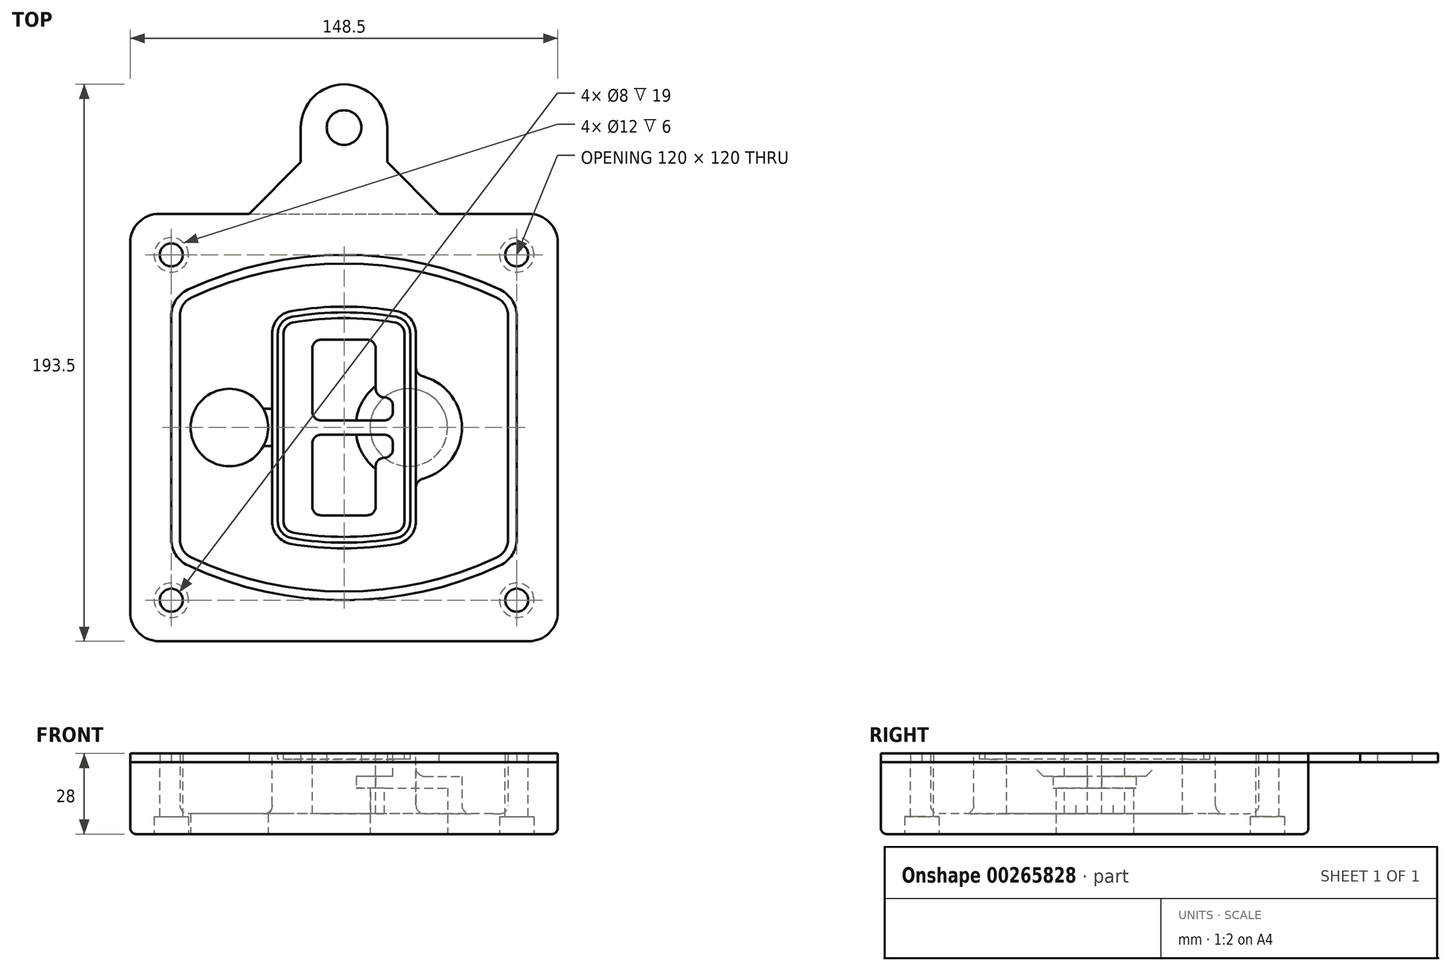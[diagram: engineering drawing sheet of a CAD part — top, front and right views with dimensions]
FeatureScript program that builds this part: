
annotation { "Feature Type Name" : "Feature", "Feature Type Description" : "" }
export const myFeature = defineFeature(function(context is Context, id is Id, definition is map)
    precondition{}
    {
        {
            var Q0;
            Q0=qCreatedBy(makeId("Top.planeOp"),FACE);
            var sketch = newSketch(context, id + "F0", { "sketchPlane" : qUnion([Q0])});
            skPoint(sketch, "E0.rect.middle", {"position": v(0, 0) * mm});
            skLineSegment(sketch, "E1.bottom", {"start": v(-64.25, -74.25) * mm, "end": v(64.25, -74.25) * mm});
            skLineSegment(sketch, "E1.top", {"start": v(-64.25, 74.25) * mm, "end": v(64.25, 74.25) * mm});
            skLineSegment(sketch, "E1.left", {"start": v(-74.25, -64.25) * mm, "end": v(-74.25, 64.25) * mm});
            skLineSegment(sketch, "E1.right", {"start": v(74.25, -64.25) * mm, "end": v(74.25, 64.25) * mm});
            skLineSegment(sketch, "E2", {"start": v(-74.25, 74.25) * mm, "end": v(74.25, -74.25) * mm, "construction": true});
            skLineSegment(sketch, "E3", {"start": v(74.25, 74.25) * mm, "end": v(-74.25, -74.25) * mm, "construction": true});
            skCircle(sketch, "E4", {"center": v(-60, 60) * mm, "radius": 4 * mm});
            skCircle(sketch, "E5", {"center": v(60, 60) * mm, "radius": 4 * mm});
            skCircle(sketch, "E6", {"center": v(60, -60) * mm, "radius": 4 * mm});
            skCircle(sketch, "E7", {"center": v(-60, -60) * mm, "radius": 4 * mm});
            skLineSegment(sketch, "E8", {"start": v(-60, 60) * mm, "end": v(60, 60) * mm, "construction": true});
            skLineSegment(sketch, "E9", {"start": v(60, 60) * mm, "end": v(60, -60) * mm, "construction": true});
            skLineSegment(sketch, "E10", {"start": v(60, -60) * mm, "end": v(-60, -60) * mm, "construction": true});
            skLineSegment(sketch, "E11", {"start": v(-60, -60) * mm, "end": v(-60, 60) * mm, "construction": true});
            skLineSegment(sketch, "E12", {"start": v(-60, 38.83) * mm, "end": v(-60, -38.83) * mm});
            skLineSegment(sketch, "E13", {"start": v(60, 38.83) * mm, "end": v(60, -38.83) * mm});
            skArc(sketch, "E14", {"start": v(54.26, 47.88) * mm, "mid": v(0, 60) * mm, "end": v(-54.26, 47.88) * mm});
            skArc(sketch, "E15", {"start": v(-54.26, -47.88) * mm, "mid": v(0, -60) * mm, "end": v(54.26, -47.88) * mm});
            skLineSegment(sketch, "E16", {"start": v(-60, 0) * mm, "end": v(60, 0) * mm, "construction": true});
            skPoint(sketch, "E17.visualSharp", {"position": v(-60, -45) * mm});
            skArc(sketch, "E17.filletArc", {"start": v(-60, -38.83) * mm, "mid": v(-58.44, -44.2) * mm, "end": v(-54.26, -47.88) * mm});
            skPoint(sketch, "E18.visualSharp", {"position": v(-60, 45) * mm});
            skArc(sketch, "E18.filletArc", {"start": v(-54.26, 47.88) * mm, "mid": v(-58.44, 44.2) * mm, "end": v(-60, 38.83) * mm});
            skPoint(sketch, "E19.visualSharp", {"position": v(60, 45) * mm});
            skArc(sketch, "E19.filletArc", {"start": v(60, 38.83) * mm, "mid": v(58.44, 44.2) * mm, "end": v(54.26, 47.88) * mm});
            skPoint(sketch, "E20.visualSharp", {"position": v(60, -45) * mm});
            skArc(sketch, "E20.filletArc", {"start": v(54.26, -47.88) * mm, "mid": v(58.44, -44.2) * mm, "end": v(60, -38.83) * mm});
            skPoint(sketch, "E21.visualSharp", {"position": v(-74.25, 74.25) * mm});
            skArc(sketch, "E21.filletArc", {"start": v(-64.25, 74.25) * mm, "mid": v(-71.32, 71.32) * mm, "end": v(-74.25, 64.25) * mm});
            skPoint(sketch, "E22.visualSharp", {"position": v(74.25, 74.25) * mm});
            skArc(sketch, "E22.filletArc", {"start": v(74.25, 64.25) * mm, "mid": v(71.32, 71.32) * mm, "end": v(64.25, 74.25) * mm});
            skPoint(sketch, "E23.visualSharp", {"position": v(74.25, -74.25) * mm});
            skArc(sketch, "E23.filletArc", {"start": v(64.25, -74.25) * mm, "mid": v(71.32, -71.32) * mm, "end": v(74.25, -64.25) * mm});
            skPoint(sketch, "E24.visualSharp", {"position": v(-74.25, -74.25) * mm});
            skArc(sketch, "E24.filletArc", {"start": v(-74.25, -64.25) * mm, "mid": v(-71.32, -71.32) * mm, "end": v(-64.25, -74.25) * mm});
            skArc(sketch, "E25.0", {"start": v(57, 38.83) * mm, "mid": v(55.9, 42.58) * mm, "end": v(52.98, 45.17) * mm});
            skLineSegment(sketch, "E25.1", {"start": v(57, 38.83) * mm, "end": v(57, -38.83) * mm});
            skArc(sketch, "E25.2", {"start": v(52.98, -45.17) * mm, "mid": v(55.9, -42.58) * mm, "end": v(57, -38.83) * mm});
            skArc(sketch, "E25.3", {"start": v(-52.98, -45.17) * mm, "mid": v(0, -57) * mm, "end": v(52.98, -45.17) * mm});
            skArc(sketch, "E25.4", {"start": v(-57, -38.83) * mm, "mid": v(-55.9, -42.58) * mm, "end": v(-52.98, -45.17) * mm});
            skArc(sketch, "E25.5", {"start": v(52.98, 45.17) * mm, "mid": v(0, 57) * mm, "end": v(-52.98, 45.17) * mm});
            skLineSegment(sketch, "E25.6", {"start": v(-57, 38.83) * mm, "end": v(-57, -38.83) * mm});
            skArc(sketch, "E25.7", {"start": v(-52.98, 45.17) * mm, "mid": v(-55.9, 42.58) * mm, "end": v(-57, 38.83) * mm});
            skArc(sketch, "E26.0", {"start": v(-55.96, 51.5) * mm, "mid": v(-61.82, 46.33) * mm, "end": v(-64, 38.83) * mm});
            skArc(sketch, "E26.1", {"start": v(55.96, 51.5) * mm, "mid": v(0, 64) * mm, "end": v(-55.96, 51.5) * mm});
            skArc(sketch, "E26.2", {"start": v(64, 38.83) * mm, "mid": v(61.82, 46.33) * mm, "end": v(55.96, 51.5) * mm});
            skLineSegment(sketch, "E26.3", {"start": v(64, 38.83) * mm, "end": v(64, -38.83) * mm});
            skArc(sketch, "E26.4", {"start": v(55.96, -51.5) * mm, "mid": v(61.82, -46.33) * mm, "end": v(64, -38.83) * mm});
            skLineSegment(sketch, "E26.5", {"start": v(-64, 38.83) * mm, "end": v(-64, -38.83) * mm});
            skArc(sketch, "E26.6", {"start": v(-55.96, -51.5) * mm, "mid": v(0, -64) * mm, "end": v(55.96, -51.5) * mm});
            skArc(sketch, "E26.7", {"start": v(-64, -38.83) * mm, "mid": v(-61.82, -46.33) * mm, "end": v(-55.96, -51.5) * mm});
            skSolve(sketch);
        }
        {
            var Q0;
            Q0=makeQuery(id+"F0.imprint","IMPRINT",FACE,{"disambiguationData":[TD([[makeQuery(id+"F0.imprint","IMPRINT",EDGE,{"derivedFrom":sQuery(id+"F0.wireOp",EDGE,"E1.bottom")}),1.0]])]});
            var Q1;
            Q1=makeQuery(id+"F0.imprint","IMPRINT",FACE,{"disambiguationData":[TD([[makeQuery(id+"F0.imprint","IMPRINT",EDGE,{"derivedFrom":sQuery(id+"F0.wireOp",EDGE,"E12")}),1.0]])]});
            var Q2;
            Q2=makeQuery(id+"F0.imprint","IMPRINT",FACE,{"disambiguationData":[TD([[makeQuery(id+"F0.imprint","IMPRINT",EDGE,{"derivedFrom":sQuery(id+"F0.wireOp",EDGE,"E25.0")}),1.0]])]});
            var Q3;
            Q3=makeQuery(id+"F0.imprint","IMPRINT",FACE,{"disambiguationData":[TD([[makeQuery(id+"F0.imprint","IMPRINT",EDGE,{"derivedFrom":sQuery(id+"F0.wireOp",EDGE,"E12")}),-1.0]])]});
            extrude(context, id + "F1", {"entities" : qUnion([Q0, Q1, Q2, Q3]), "oppositeDirection" : true, "depth" : 25 * mm});
        }
        {
            var Q0;
            Q0=makeQuery(id+"F0.imprint","IMPRINT",FACE,{"disambiguationData":[TD([[makeQuery(id+"F0.imprint","IMPRINT",EDGE,{"derivedFrom":sQuery(id+"F0.wireOp",EDGE,"E12")}),1.0]])]});
            extrude(context, id + "F2", {"entities" : qUnion([Q0]), "operationType" : NewBodyOperationType.ADD, "depth" : 3 * mm});
        }
        {
            var Q0;
            Q0=makeQuery(id+"F0.imprint","IMPRINT",FACE,{"disambiguationData":[TD([[makeQuery(id+"F0.imprint","IMPRINT",EDGE,{"derivedFrom":sQuery(id+"F0.wireOp",EDGE,"E25.0")}),1.0]])]});
            extrude(context, id + "F3", {"entities" : qUnion([Q0]), "operationType" : NewBodyOperationType.REMOVE, "oppositeDirection" : true, "depth" : 18 * mm});
        }
        {
            var Q0;
            Q0=makeQuery(id+"F2.opExtrude","CAP_FACE",FACE,{"disambiguationData":[OSD([sQuery(id+"F0.wireOp",EDGE,"E12"),sQuery(id+"F0.wireOp",EDGE,"E13"),sQuery(id+"F0.wireOp",EDGE,"E14"),sQuery(id+"F0.wireOp",EDGE,"E15"),sQuery(id+"F0.wireOp",EDGE,"E17.filletArc"),sQuery(id+"F0.wireOp",EDGE,"E18.filletArc"),sQuery(id+"F0.wireOp",EDGE,"E19.filletArc"),sQuery(id+"F0.wireOp",EDGE,"E20.filletArc"),sQuery(id+"F0.wireOp",EDGE,"E25.0"),sQuery(id+"F0.wireOp",EDGE,"E25.1"),sQuery(id+"F0.wireOp",EDGE,"E25.2"),sQuery(id+"F0.wireOp",EDGE,"E25.3"),sQuery(id+"F0.wireOp",EDGE,"E25.4"),sQuery(id+"F0.wireOp",EDGE,"E25.5"),sQuery(id+"F0.wireOp",EDGE,"E25.6"),sQuery(id+"F0.wireOp",EDGE,"E25.7")])],"isStart":false});
            var sketch = newSketch(context, id + "F4", { "sketchPlane" : qUnion([Q0])});
            skArc(sketch, "E27.0", {"start": v(-18.34, -40.45) * mm, "mid": v(0, -42) * mm, "end": v(18.34, -40.45) * mm});
            skArc(sketch, "E28.0", {"start": v(18.34, 40.45) * mm, "mid": v(0, 42) * mm, "end": v(-18.34, 40.45) * mm});
            skLineSegment(sketch, "E29", {"start": v(-25, 32.57) * mm, "end": v(-25, -32.57) * mm});
            skLineSegment(sketch, "E30", {"start": v(25, 32.57) * mm, "end": v(25, -32.57) * mm});
            skLineSegment(sketch, "E31", {"start": v(-25, 39.1) * mm, "end": v(25, 39.1) * mm, "construction": true});
            skLineSegment(sketch, "E32", {"start": v(-25, -39.1) * mm, "end": v(25, -39.1) * mm, "construction": true});
            skPoint(sketch, "E33.visualSharp", {"position": v(-25, 39.1) * mm});
            skArc(sketch, "E33.filletArc", {"start": v(-18.34, 40.45) * mm, "mid": v(-23.11, 37.73) * mm, "end": v(-25, 32.57) * mm});
            skPoint(sketch, "E34.visualSharp", {"position": v(25, 39.1) * mm});
            skArc(sketch, "E34.filletArc", {"start": v(25, 32.57) * mm, "mid": v(23.11, 37.73) * mm, "end": v(18.34, 40.45) * mm});
            skPoint(sketch, "E35.visualSharp", {"position": v(25, -39.1) * mm});
            skArc(sketch, "E35.filletArc", {"start": v(18.34, -40.45) * mm, "mid": v(23.11, -37.73) * mm, "end": v(25, -32.57) * mm});
            skPoint(sketch, "E36.visualSharp", {"position": v(-25, -39.1) * mm});
            skArc(sketch, "E36.filletArc", {"start": v(-25, -32.57) * mm, "mid": v(-23.11, -37.73) * mm, "end": v(-18.34, -40.45) * mm});
            skArc(sketch, "E37.0", {"start": v(52.98, 45.17) * mm, "mid": v(0, 57) * mm, "end": v(-52.98, 45.17) * mm});
            skArc(sketch, "E37.1", {"start": v(-52.98, 45.17) * mm, "mid": v(-55.9, 42.58) * mm, "end": v(-57, 38.83) * mm});
            skLineSegment(sketch, "E37.2", {"start": v(-57, 38.83) * mm, "end": v(-57, -38.83) * mm});
            skArc(sketch, "E37.3", {"start": v(-57, -38.83) * mm, "mid": v(-55.9, -42.58) * mm, "end": v(-52.98, -45.17) * mm});
            skArc(sketch, "E37.4", {"start": v(-52.98, -45.17) * mm, "mid": v(0, -57) * mm, "end": v(52.98, -45.17) * mm});
            skArc(sketch, "E37.5", {"start": v(52.98, -45.17) * mm, "mid": v(55.9, -42.58) * mm, "end": v(57, -38.83) * mm});
            skLineSegment(sketch, "E37.6", {"start": v(57, 38.83) * mm, "end": v(57, -38.83) * mm});
            skArc(sketch, "E37.7", {"start": v(57, 38.83) * mm, "mid": v(55.9, 42.58) * mm, "end": v(52.98, 45.17) * mm});
            skLineSegment(sketch, "E38.0", {"start": v(23, 32.57) * mm, "end": v(23, -32.57) * mm});
            skArc(sketch, "E38.1", {"start": v(18, -38.48) * mm, "mid": v(21.58, -36.44) * mm, "end": v(23, -32.57) * mm});
            skArc(sketch, "E38.2", {"start": v(-18, -38.48) * mm, "mid": v(0, -40) * mm, "end": v(18, -38.48) * mm});
            skArc(sketch, "E38.3", {"start": v(-23, -32.57) * mm, "mid": v(-21.58, -36.44) * mm, "end": v(-18, -38.48) * mm});
            skLineSegment(sketch, "E38.4", {"start": v(-23, 32.57) * mm, "end": v(-23, -32.57) * mm});
            skArc(sketch, "E38.5", {"start": v(23, 32.57) * mm, "mid": v(21.58, 36.44) * mm, "end": v(18, 38.48) * mm});
            skArc(sketch, "E38.6", {"start": v(-18, 38.48) * mm, "mid": v(-21.58, 36.44) * mm, "end": v(-23, 32.57) * mm});
            skArc(sketch, "E38.7", {"start": v(18, 38.48) * mm, "mid": v(0, 40) * mm, "end": v(-18, 38.48) * mm});
            skArc(sketch, "E39.0", {"start": v(21, 32.57) * mm, "mid": v(20.06, 35.15) * mm, "end": v(17.67, 36.5) * mm});
            skLineSegment(sketch, "E39.1", {"start": v(21, 32.57) * mm, "end": v(21, -32.57) * mm});
            skArc(sketch, "E39.2", {"start": v(17.67, -36.5) * mm, "mid": v(20.06, -35.15) * mm, "end": v(21, -32.57) * mm});
            skArc(sketch, "E39.3", {"start": v(-17.67, -36.5) * mm, "mid": v(0, -38) * mm, "end": v(17.67, -36.5) * mm});
            skArc(sketch, "E39.4", {"start": v(-21, -32.57) * mm, "mid": v(-20.06, -35.15) * mm, "end": v(-17.67, -36.5) * mm});
            skArc(sketch, "E39.5", {"start": v(17.67, 36.5) * mm, "mid": v(0, 38) * mm, "end": v(-17.67, 36.5) * mm});
            skLineSegment(sketch, "E39.6", {"start": v(-21, 32.57) * mm, "end": v(-21, -32.57) * mm});
            skArc(sketch, "E39.7", {"start": v(-17.67, 36.5) * mm, "mid": v(-20.06, 35.15) * mm, "end": v(-21, 32.57) * mm});
            skLineSegment(sketch, "E40", {"start": v(-25, 0) * mm, "end": v(25, 0) * mm, "construction": true});
            skLineSegment(sketch, "E41", {"start": v(-11, 5.5) * mm, "end": v(-11, 27.5) * mm});
            skLineSegment(sketch, "E42", {"start": v(-8, 30.5) * mm, "end": v(8, 30.5) * mm});
            skLineSegment(sketch, "E43", {"start": v(11, 27.5) * mm, "end": v(11, 13.5) * mm});
            skLineSegment(sketch, "E44", {"start": v(14, 10.5) * mm, "end": v(14, 10.5) * mm});
            skLineSegment(sketch, "E45", {"start": v(17, 7.5) * mm, "end": v(17, 5.5) * mm});
            skLineSegment(sketch, "E46", {"start": v(14, 2.5) * mm, "end": v(-8, 2.5) * mm});
            skPoint(sketch, "E47.visualSharp", {"position": v(-11, 30.5) * mm});
            skArc(sketch, "E47.filletArc", {"start": v(-8, 30.5) * mm, "mid": v(-10.12, 29.62) * mm, "end": v(-11, 27.5) * mm});
            skPoint(sketch, "E48.visualSharp", {"position": v(11, 30.5) * mm});
            skArc(sketch, "E48.filletArc", {"start": v(11, 27.5) * mm, "mid": v(10.12, 29.62) * mm, "end": v(8, 30.5) * mm});
            skPoint(sketch, "E49.visualSharp", {"position": v(11, 10.5) * mm});
            skArc(sketch, "E49.filletArc", {"start": v(11, 13.5) * mm, "mid": v(11.88, 11.38) * mm, "end": v(14, 10.5) * mm});
            skPoint(sketch, "E50.visualSharp", {"position": v(17, 10.5) * mm});
            skArc(sketch, "E50.filletArc", {"start": v(17, 7.5) * mm, "mid": v(16.12, 9.62) * mm, "end": v(14, 10.5) * mm});
            skPoint(sketch, "E51.visualSharp", {"position": v(17, 2.5) * mm});
            skArc(sketch, "E51.filletArc", {"start": v(14, 2.5) * mm, "mid": v(16.12, 3.38) * mm, "end": v(17, 5.5) * mm});
            skPoint(sketch, "E52.visualSharp", {"position": v(-11, 2.5) * mm});
            skArc(sketch, "E52.filletArc", {"start": v(-11, 5.5) * mm, "mid": v(-10.12, 3.38) * mm, "end": v(-8, 2.5) * mm});
            skLineSegment(sketch, "E53.0.MirrorCS", {"start": v(14, -2.5) * mm, "end": v(-8, -2.5) * mm});
            skArc(sketch, "E54.0.MirrorCS", {"start": v(-11, -5.5) * mm, "mid": v(-10.12, -3.38) * mm, "end": v(-8, -2.5) * mm});
            skLineSegment(sketch, "E55.0.MirrorCS", {"start": v(-11, -5.5) * mm, "end": v(-11, -27.5) * mm});
            skArc(sketch, "E56.0.MirrorCS", {"start": v(-8, -30.5) * mm, "mid": v(-10.12, -29.62) * mm, "end": v(-11, -27.5) * mm});
            skLineSegment(sketch, "E57.0.MirrorCS", {"start": v(-8, -30.5) * mm, "end": v(8, -30.5) * mm});
            skArc(sketch, "E58.0.MirrorCS", {"start": v(11, -27.5) * mm, "mid": v(10.12, -29.62) * mm, "end": v(8, -30.5) * mm});
            skLineSegment(sketch, "E59.0.MirrorCS", {"start": v(11, -27.5) * mm, "end": v(11, -13.5) * mm});
            skArc(sketch, "E60.0.MirrorCS", {"start": v(11, -13.5) * mm, "mid": v(11.88, -11.38) * mm, "end": v(14, -10.5) * mm});
            skArc(sketch, "E61.0.MirrorCS", {"start": v(17, -7.5) * mm, "mid": v(16.12, -9.62) * mm, "end": v(14, -10.5) * mm});
            skLineSegment(sketch, "E62.0.MirrorCS", {"start": v(17, -7.5) * mm, "end": v(17, -5.5) * mm});
            skArc(sketch, "E63.0.MirrorCS", {"start": v(14, -2.5) * mm, "mid": v(16.12, -3.38) * mm, "end": v(17, -5.5) * mm});
            skSolve(sketch);
        }
        {
            var Q0;
            Q0=makeQuery(id+"F4.imprint","IMPRINT",FACE,{"disambiguationData":[TD([[makeQuery(id+"F4.imprint","IMPRINT",EDGE,{"derivedFrom":sQuery(id+"F4.wireOp",EDGE,"E27.0")}),1.0]])]});
            var Q1;
            Q1=makeQuery(id+"F4.imprint","IMPRINT",FACE,{"disambiguationData":[TD([[makeQuery(id+"F4.imprint","IMPRINT",EDGE,{"derivedFrom":sQuery(id+"F4.wireOp",EDGE,"E38.0")}),-1.0]])]});
            var Q2;
            Q2=makeQuery(id+"F4.imprint","IMPRINT",FACE,{"disambiguationData":[TD([[makeQuery(id+"F4.imprint","IMPRINT",EDGE,{"derivedFrom":sQuery(id+"F4.wireOp",EDGE,"E39.0")}),1.0]])]});
            extrude(context, id + "F5", {"entities" : qUnion([Q0, Q1, Q2]), "operationType" : NewBodyOperationType.ADD, "endBound" : BoundingType.UP_TO_NEXT, "oppositeDirection" : true, "depth" : 25 * mm});
        }
        {
            var Q0;
            Q0=makeQuery(id+"F4.imprint","IMPRINT",FACE,{"disambiguationData":[TD([[makeQuery(id+"F4.imprint","IMPRINT",EDGE,{"derivedFrom":sQuery(id+"F4.wireOp",EDGE,"E38.0")}),-1.0]])]});
            extrude(context, id + "F6", {"entities" : qUnion([Q0]), "operationType" : NewBodyOperationType.REMOVE, "oppositeDirection" : true, "depth" : 2 * mm});
        }
        {
            var Q0;
            Q0=makeQuery(id+"F1.opExtrude","CAP_FACE",FACE,{"disambiguationData":[OSD([sQuery(id+"F0.wireOp",EDGE,"E1.bottom"),sQuery(id+"F0.wireOp",EDGE,"E1.top"),sQuery(id+"F0.wireOp",EDGE,"E1.left"),sQuery(id+"F0.wireOp",EDGE,"E1.right"),sQuery(id+"F0.wireOp",EDGE,"E4"),sQuery(id+"F0.wireOp",EDGE,"E5"),sQuery(id+"F0.wireOp",EDGE,"E6"),sQuery(id+"F0.wireOp",EDGE,"E7"),sQuery(id+"F0.wireOp",EDGE,"E21.filletArc"),sQuery(id+"F0.wireOp",EDGE,"E22.filletArc"),sQuery(id+"F0.wireOp",EDGE,"E23.filletArc"),sQuery(id+"F0.wireOp",EDGE,"E24.filletArc")])],"isStart":false});
            var sketch = newSketch(context, id + "F7", { "sketchPlane" : qUnion([Q0])});
            skCircle(sketch, "E64", {"center": v(22.5, 0) * mm, "radius": 13.47 * mm});
            skCircle(sketch, "E65", {"center": v(-39.81, 0) * mm, "radius": 13.47 * mm});
            skLineSegment(sketch, "E66", {"start": v(74.25, 0) * mm, "end": v(-74.25, 0) * mm});
            skCircle(sketch, "E67", {"center": v(22.5, 0) * mm, "radius": 18.47 * mm});
            skCircle(sketch, "E68", {"center": v(60, -60) * mm, "radius": 6 * mm});
            skCircle(sketch, "E69", {"center": v(-60, -60) * mm, "radius": 6 * mm});
            skCircle(sketch, "E70", {"center": v(-60, 60) * mm, "radius": 6 * mm});
            skCircle(sketch, "E71", {"center": v(60, 60) * mm, "radius": 6 * mm});
            skSolve(sketch);
        }
        {
            var Q0;
            {var subQ1=sQuery(id+"F7.wireOp",EDGE,"E66");var subQ4=sQuery(id+"F7.wireOp",EDGE,"E64");var subQ6=makeQuery(id+"F7.imprint","INTERSECT",VERTEX,{"disambiguationData":[OD(0.0)],"derivedFrom":[subQ4,subQ1]});Q0=makeQuery(id+"F7.imprint","IMPRINT",FACE,{"disambiguationData":[TD([[makeQuery(id+"F7.imprint","IMPRINT",EDGE,{"disambiguationData":[TD([[subQ6,-1.0]])],"derivedFrom":subQ4}),-1.0]])]});}
            var Q1;
            {var subQ0=sQuery(id+"F7.wireOp",EDGE,"E66");var subQ1=sQuery(id+"F7.wireOp",EDGE,"E64");var subQ3=makeQuery(id+"F7.imprint","INTERSECT",VERTEX,{"disambiguationData":[OD(0.0)],"derivedFrom":[subQ1,subQ0]});Q1=makeQuery(id+"F7.imprint","IMPRINT",FACE,{"disambiguationData":[TD([[makeQuery(id+"F7.imprint","IMPRINT",EDGE,{"disambiguationData":[TD([[subQ3,-1.0]])],"derivedFrom":subQ1}),1.0]])]});}
            var Q2;
            {var subQ0=sQuery(id+"F7.wireOp",EDGE,"E66");var subQ1=sQuery(id+"F7.wireOp",EDGE,"E64");var subQ3=makeQuery(id+"F7.imprint","INTERSECT",VERTEX,{"disambiguationData":[OD(0.0)],"derivedFrom":[subQ1,subQ0]});Q2=makeQuery(id+"F7.imprint","IMPRINT",FACE,{"disambiguationData":[TD([[makeQuery(id+"F7.imprint","IMPRINT",EDGE,{"disambiguationData":[TD([[subQ3,1.0]])],"derivedFrom":subQ1}),1.0]])]});}
            var Q3;
            {var subQ1=sQuery(id+"F7.wireOp",EDGE,"E66");var subQ4=sQuery(id+"F7.wireOp",EDGE,"E64");var subQ6=makeQuery(id+"F7.imprint","INTERSECT",VERTEX,{"disambiguationData":[OD(0.0)],"derivedFrom":[subQ4,subQ1]});Q3=makeQuery(id+"F7.imprint","IMPRINT",FACE,{"disambiguationData":[TD([[makeQuery(id+"F7.imprint","IMPRINT",EDGE,{"disambiguationData":[TD([[subQ6,1.0]])],"derivedFrom":subQ4}),-1.0]])]});}
            extrude(context, id + "F8", {"entities" : qUnion([Q0, Q1, Q2, Q3]), "operationType" : NewBodyOperationType.ADD, "oppositeDirection" : true, "depth" : 20 * mm});
        }
        {
            var Q0;
            {var subQ0=sQuery(id+"F7.wireOp",EDGE,"E66");var subQ1=sQuery(id+"F7.wireOp",EDGE,"E64");var subQ3=makeQuery(id+"F7.imprint","INTERSECT",VERTEX,{"disambiguationData":[OD(0.0)],"derivedFrom":[subQ1,subQ0]});Q0=makeQuery(id+"F7.imprint","IMPRINT",FACE,{"disambiguationData":[TD([[makeQuery(id+"F7.imprint","IMPRINT",EDGE,{"disambiguationData":[TD([[subQ3,-1.0]])],"derivedFrom":subQ1}),1.0]])]});}
            var Q1;
            {var subQ0=sQuery(id+"F7.wireOp",EDGE,"E66");var subQ1=sQuery(id+"F7.wireOp",EDGE,"E64");var subQ3=makeQuery(id+"F7.imprint","INTERSECT",VERTEX,{"disambiguationData":[OD(0.0)],"derivedFrom":[subQ1,subQ0]});Q1=makeQuery(id+"F7.imprint","IMPRINT",FACE,{"disambiguationData":[TD([[makeQuery(id+"F7.imprint","IMPRINT",EDGE,{"disambiguationData":[TD([[subQ3,1.0]])],"derivedFrom":subQ1}),1.0]])]});}
            extrude(context, id + "F9", {"entities" : qUnion([Q0, Q1]), "operationType" : NewBodyOperationType.REMOVE, "oppositeDirection" : true, "depth" : 16 * mm});
        }
        {
            var Q0;
            {var subQ0=sQuery(id+"F7.wireOp",EDGE,"E66");var subQ1=sQuery(id+"F7.wireOp",EDGE,"E65");var subQ3=makeQuery(id+"F7.imprint","INTERSECT",VERTEX,{"disambiguationData":[OD(0.0)],"derivedFrom":[subQ1,subQ0]});Q0=makeQuery(id+"F7.imprint","IMPRINT",FACE,{"disambiguationData":[TD([[makeQuery(id+"F7.imprint","IMPRINT",EDGE,{"disambiguationData":[TD([[subQ3,-1.0]])],"derivedFrom":subQ1}),1.0]])]});}
            var Q1;
            {var subQ0=sQuery(id+"F7.wireOp",EDGE,"E66");var subQ1=sQuery(id+"F7.wireOp",EDGE,"E65");var subQ3=makeQuery(id+"F7.imprint","INTERSECT",VERTEX,{"disambiguationData":[OD(0.0)],"derivedFrom":[subQ1,subQ0]});Q1=makeQuery(id+"F7.imprint","IMPRINT",FACE,{"disambiguationData":[TD([[makeQuery(id+"F7.imprint","IMPRINT",EDGE,{"disambiguationData":[TD([[subQ3,1.0]])],"derivedFrom":subQ1}),1.0]])]});}
            extrude(context, id + "F10", {"entities" : qUnion([Q0, Q1]), "operationType" : NewBodyOperationType.REMOVE, "oppositeDirection" : true, "depth" : 25 * mm});
        }
        {
            var Q0;
            Q0=makeQuery(id+"F7.imprint","IMPRINT",FACE,{"disambiguationData":[TD([[makeQuery(id+"F7.imprint","IMPRINT",EDGE,{"derivedFrom":sQuery(id+"F7.wireOp",EDGE,"E68")}),1.0]])]});
            var Q1;
            Q1=makeQuery(id+"F7.imprint","IMPRINT",FACE,{"disambiguationData":[TD([[makeQuery(id+"F7.imprint","IMPRINT",EDGE,{"derivedFrom":makeQuery(id+"F1.opExtrude","CAP_EDGE",EDGE,{"disambiguationData":[OSD([sQuery(id+"F0.wireOp",EDGE,"E5")])],"isStart":false})}),-1.0]])]});
            var Q2;
            Q2=makeQuery(id+"F7.imprint","IMPRINT",FACE,{"disambiguationData":[TD([[makeQuery(id+"F7.imprint","IMPRINT",EDGE,{"derivedFrom":sQuery(id+"F7.wireOp",EDGE,"E69")}),1.0]])]});
            var Q3;
            Q3=makeQuery(id+"F7.imprint","IMPRINT",FACE,{"disambiguationData":[TD([[makeQuery(id+"F7.imprint","IMPRINT",EDGE,{"derivedFrom":makeQuery(id+"F1.opExtrude","CAP_EDGE",EDGE,{"disambiguationData":[OSD([sQuery(id+"F0.wireOp",EDGE,"E4")])],"isStart":false})}),-1.0]])]});
            var Q4;
            Q4=makeQuery(id+"F7.imprint","IMPRINT",FACE,{"disambiguationData":[TD([[makeQuery(id+"F7.imprint","IMPRINT",EDGE,{"derivedFrom":sQuery(id+"F7.wireOp",EDGE,"E70")}),1.0]])]});
            var Q5;
            Q5=makeQuery(id+"F7.imprint","IMPRINT",FACE,{"disambiguationData":[TD([[makeQuery(id+"F7.imprint","IMPRINT",EDGE,{"derivedFrom":makeQuery(id+"F1.opExtrude","CAP_EDGE",EDGE,{"disambiguationData":[OSD([sQuery(id+"F0.wireOp",EDGE,"E7")])],"isStart":false})}),-1.0]])]});
            var Q6;
            Q6=makeQuery(id+"F7.imprint","IMPRINT",FACE,{"disambiguationData":[TD([[makeQuery(id+"F7.imprint","IMPRINT",EDGE,{"derivedFrom":sQuery(id+"F7.wireOp",EDGE,"E71")}),1.0]])]});
            var Q7;
            Q7=makeQuery(id+"F7.imprint","IMPRINT",FACE,{"disambiguationData":[TD([[makeQuery(id+"F7.imprint","IMPRINT",EDGE,{"derivedFrom":makeQuery(id+"F1.opExtrude","CAP_EDGE",EDGE,{"disambiguationData":[OSD([sQuery(id+"F0.wireOp",EDGE,"E6")])],"isStart":false})}),-1.0]])]});
            extrude(context, id + "F11", {"entities" : qUnion([Q0, Q1, Q2, Q3, Q4, Q5, Q6, Q7]), "operationType" : NewBodyOperationType.REMOVE, "oppositeDirection" : true, "depth" : 6 * mm});
        }
        {
            var Q0;
            Q0=makeQuery(id+"F9.boolean.opBoolean","COPY",FACE,{"derivedFrom":makeQuery(id+"F9.opExtrude","CAP_FACE",FACE,{"disambiguationData":[OSD([sQuery(id+"F7.wireOp",EDGE,"E64")])],"isStart":false})});
            var sketch = newSketch(context, id + "F12", { "sketchPlane" : qUnion([Q0])});
            skArc(sketch, "E72.0", {"start": v(11, 14.45) * mm, "mid": v(6.45, 9.13) * mm, "end": v(4.2, 2.5) * mm});
            skArc(sketch, "E72.1", {"start": v(4.2, -2.5) * mm, "mid": v(6.45, -9.13) * mm, "end": v(11, -14.45) * mm});
            skLineSegment(sketch, "E73", {"start": v(4.2, -2.5) * mm, "end": v(14, -2.5) * mm});
            skLineSegment(sketch, "E74.0", {"start": v(14, 2.5) * mm, "end": v(4.2, 2.5) * mm});
            skArc(sketch, "E74.1", {"start": v(14, 2.5) * mm, "mid": v(16.12, 3.38) * mm, "end": v(17, 5.5) * mm});
            skLineSegment(sketch, "E74.2", {"start": v(17, 7.5) * mm, "end": v(17, 5.5) * mm});
            skArc(sketch, "E74.3", {"start": v(17, 7.5) * mm, "mid": v(16.12, 9.62) * mm, "end": v(14, 10.5) * mm});
            skArc(sketch, "E74.4", {"start": v(11, 13.5) * mm, "mid": v(11.88, 11.38) * mm, "end": v(14, 10.5) * mm});
            skLineSegment(sketch, "E74.5", {"start": v(11, 14.45) * mm, "end": v(11, 13.5) * mm});
            skLineSegment(sketch, "E74.7", {"start": v(14, -2.5) * mm, "end": v(4.2, -2.5) * mm});
            skArc(sketch, "E74.8", {"start": v(14, -2.5) * mm, "mid": v(16.12, -3.38) * mm, "end": v(17, -5.5) * mm});
            skLineSegment(sketch, "E74.9", {"start": v(17, -7.5) * mm, "end": v(17, -5.5) * mm});
            skArc(sketch, "E74.10", {"start": v(17, -7.5) * mm, "mid": v(16.12, -9.62) * mm, "end": v(14, -10.5) * mm});
            skArc(sketch, "E74.11", {"start": v(11, -13.5) * mm, "mid": v(11.88, -11.38) * mm, "end": v(14, -10.5) * mm});
            skLineSegment(sketch, "E74.12", {"start": v(11, -14.45) * mm, "end": v(11, -13.5) * mm});
            skPoint(sketch, "E75.orphan", {"position": v(11, -27.5) * mm});
            skPoint(sketch, "E76.orphan", {"position": v(-8, -2.5) * mm});
            skPoint(sketch, "E77.orphan", {"position": v(-8, 2.5) * mm});
            skPoint(sketch, "E78.orphan", {"position": v(11, 27.5) * mm});
            skSolve(sketch);
        }
        {
            var Q0;
            {var subQ7=sQuery(id+"F12.wireOp",EDGE,"E72.0");var subQ14=sQuery(id+"F12.wireOp",EDGE,"E72.1");var subQ16=sQuery(id+"F12.wireOp",EDGE,"E74.1");var subQ18=sQuery(id+"F12.wireOp",EDGE,"E74.8");Q0=qUnion([makeQuery(id+"F12.imprint","IMPRINT",FACE,{"disambiguationData":[TD([[makeQuery(id+"F12.imprint","IMPRINT",EDGE,{"derivedFrom":subQ7}),1.0]])]}),makeQuery(id+"F12.imprint","IMPRINT",FACE,{"disambiguationData":[TD([[makeQuery(id+"F12.imprint","IMPRINT",EDGE,{"derivedFrom":subQ14}),1.0]])]}),makeQuery(id+"F12.imprint","IMPRINT",FACE,{"disambiguationData":[TD([[makeQuery(id+"F12.imprint","IMPRINT",EDGE,{"derivedFrom":subQ16}),1.0]])]}),makeQuery(id+"F12.imprint","IMPRINT",FACE,{"disambiguationData":[TD([[makeQuery(id+"F12.imprint","IMPRINT",EDGE,{"derivedFrom":subQ18}),-1.0]])]})]);}
            var Q1;
            Q1=makeQuery(id+"F5.boolean.opBoolean","SPLIT",FACE,{"disambiguationData":[TD([makeQuery(id+"F5.opExtrude","SWEPT_FACE",FACE,{"disambiguationData":[OSD([sQuery(id+"F4.wireOp",EDGE,"E41")])]})])],"derivedFrom":makeQuery(id+"F3.boolean.opBoolean","COPY",FACE,{"derivedFrom":makeQuery(id+"F3.opExtrude","CAP_FACE",FACE,{"disambiguationData":[OSD([sQuery(id+"F0.wireOp",EDGE,"E25.0"),sQuery(id+"F0.wireOp",EDGE,"E25.1"),sQuery(id+"F0.wireOp",EDGE,"E25.2"),sQuery(id+"F0.wireOp",EDGE,"E25.3"),sQuery(id+"F0.wireOp",EDGE,"E25.4"),sQuery(id+"F0.wireOp",EDGE,"E25.5"),sQuery(id+"F0.wireOp",EDGE,"E25.6"),sQuery(id+"F0.wireOp",EDGE,"E25.7")])],"isStart":false})})});
            extrude(context, id + "F13", {"entities" : qUnion([Q0]), "operationType" : NewBodyOperationType.REMOVE, "endBound" : BoundingType.UP_TO_SURFACE, "endBoundEntityFace" : qUnion([Q1]), "depth" : 25 * mm});
        }
        {
            var Q0;
            Q0=makeQuery(id+"F3.boolean.opBoolean","COPY",EDGE,{"derivedFrom":makeQuery(id+"F3.opExtrude","CAP_EDGE",EDGE,{"disambiguationData":[OSD([sQuery(id+"F0.wireOp",EDGE,"E25.6")])],"isStart":false})});
            var Q1;
            Q1=makeQuery(id+"F8.boolean.opBoolean","INTERSECT",EDGE,{"derivedFrom":[makeQuery(id+"F5.opExtrude","SWEPT_FACE",FACE,{"disambiguationData":[OSD([sQuery(id+"F4.wireOp",EDGE,"E30")])]}),makeQuery(id+"F8.opExtrude","CAP_FACE",FACE,{"disambiguationData":[OSD([sQuery(id+"F7.wireOp",EDGE,"E67")])],"isStart":false})]});
            var Q2;
            Q2=makeQuery(id+"F8.boolean.opBoolean","INTERSECT",EDGE,{"disambiguationData":[OD(1.0)],"derivedFrom":[makeQuery(id+"F5.opExtrude","SWEPT_FACE",FACE,{"disambiguationData":[OSD([sQuery(id+"F4.wireOp",EDGE,"E30")])]}),makeQuery(id+"F8.opExtrude","SWEPT_FACE",FACE,{"disambiguationData":[OSD([sQuery(id+"F7.wireOp",EDGE,"E67")])]})]});
            var Q3;
            {var subQ0=sQuery(id+"F4.wireOp",EDGE,"E30");Q3=makeQuery(id+"F8.boolean.opBoolean","SPLIT",EDGE,{"disambiguationData":[TD([makeQuery(id+"F5.opExtrude","SWEPT_FACE",FACE,{"disambiguationData":[OSD([sQuery(id+"F4.wireOp",EDGE,"E35.filletArc")])]})])],"derivedFrom":makeQuery(id+"F5.opExtrude","CAP_EDGE",EDGE,{"disambiguationData":[OSD([subQ0])],"isStart":false})});}
            var Q4;
            {var subQ0=sQuery(id+"F0.wireOp",EDGE,"E25.7");var subQ1=sQuery(id+"F0.wireOp",EDGE,"E25.1");var subQ2=sQuery(id+"F0.wireOp",EDGE,"E25.6");var subQ3=sQuery(id+"F0.wireOp",EDGE,"E25.5");var subQ4=sQuery(id+"F0.wireOp",EDGE,"E25.4");var subQ5=sQuery(id+"F0.wireOp",EDGE,"E25.0");var subQ6=sQuery(id+"F0.wireOp",EDGE,"E25.2");var subQ7=sQuery(id+"F0.wireOp",EDGE,"E25.3");Q4=makeQuery(id+"F8.boolean.opBoolean","INTERSECT",EDGE,{"derivedFrom":[makeQuery(id+"F5.boolean.opBoolean","SPLIT",FACE,{"disambiguationData":[TD([makeQuery(id+"F2.opExtrude","SWEPT_FACE",FACE,{"disambiguationData":[OSD([subQ5])]})])],"derivedFrom":makeQuery(id+"F3.boolean.opBoolean","COPY",FACE,{"derivedFrom":makeQuery(id+"F3.opExtrude","CAP_FACE",FACE,{"disambiguationData":[OSD([subQ5,subQ1,subQ6,subQ7,subQ4,subQ3,subQ2,subQ0])],"isStart":false})})}),makeQuery(id+"F8.opExtrude","SWEPT_FACE",FACE,{"disambiguationData":[OSD([sQuery(id+"F7.wireOp",EDGE,"E67")])]})]});}
            var Q5;
            Q5=makeQuery(id+"F8.boolean.opBoolean","INTERSECT",EDGE,{"disambiguationData":[OD(0.0)],"derivedFrom":[makeQuery(id+"F5.opExtrude","SWEPT_FACE",FACE,{"disambiguationData":[OSD([sQuery(id+"F4.wireOp",EDGE,"E30")])]}),makeQuery(id+"F8.opExtrude","SWEPT_FACE",FACE,{"disambiguationData":[OSD([sQuery(id+"F7.wireOp",EDGE,"E67")])]})]});
            fillet(context, id + "F14", {"entities" : qUnion([Q0, Q1, Q2, Q3, Q4, Q5]), "radius" : 3 * mm, "tangentPropagation" : true, "allowEdgeOverflow" : false});
        }
        {
            var Q0;
            Q0=makeQuery(id+"F1.opExtrude","CAP_EDGE",EDGE,{"disambiguationData":[OSD([sQuery(id+"F0.wireOp",EDGE,"E1.bottom")])],"isStart":false});
            fillet(context, id + "F15", {"entities" : qUnion([Q0]), "radius" : 2 * mm, "tangentPropagation" : true, "allowEdgeOverflow" : false});
        }
        {
            var Q0;
            {var subQ0=sQuery(id+"F0.wireOp",EDGE,"E22.filletArc");var subQ1=sQuery(id+"F0.wireOp",EDGE,"E7");var subQ2=sQuery(id+"F0.wireOp",EDGE,"E6");var subQ3=sQuery(id+"F0.wireOp",EDGE,"E5");var subQ4=sQuery(id+"F0.wireOp",EDGE,"E4");var subQ5=sQuery(id+"F0.wireOp",EDGE,"E1.bottom");var subQ6=sQuery(id+"F0.wireOp",EDGE,"E21.filletArc");var subQ7=sQuery(id+"F0.wireOp",EDGE,"E1.top");var subQ8=sQuery(id+"F0.wireOp",EDGE,"E1.left");var subQ9=sQuery(id+"F0.wireOp",EDGE,"E1.right");var subQ10=sQuery(id+"F0.wireOp",EDGE,"E23.filletArc");var subQ11=sQuery(id+"F0.wireOp",EDGE,"E24.filletArc");Q0=makeQuery(id+"F2.boolean.opBoolean","SPLIT",FACE,{"disambiguationData":[TD([makeQuery(id+"F1.opExtrude","SWEPT_FACE",FACE,{"disambiguationData":[OSD([subQ5])]})])],"derivedFrom":makeQuery(id+"F1.opExtrude","CAP_FACE",FACE,{"disambiguationData":[OSD([subQ5,subQ7,subQ8,subQ9,subQ4,subQ3,subQ2,subQ1,subQ6,subQ0,subQ10,subQ11])],"isStart":true})});}
            var sketch = newSketch(context, id + "F16", { "sketchPlane" : qUnion([Q0])});
            skLineSegment(sketch, "E79", {"start": v(0, 74.25) * mm, "end": v(0, 104.25) * mm, "construction": true});
            skPoint(sketch, "E79.endSnap0", {"position": v(0, 60) * mm});
            skCircle(sketch, "E80", {"center": v(0, 104.25) * mm, "radius": 6 * mm});
            skLineSegment(sketch, "E81", {"start": v(-33, 74.25) * mm, "end": v(-15, 92.25) * mm});
            skLineSegment(sketch, "E82", {"start": v(-15, 92.25) * mm, "end": v(-15, 104.25) * mm});
            skLineSegment(sketch, "E83", {"start": v(33, 74.25) * mm, "end": v(15, 92.25) * mm});
            skLineSegment(sketch, "E84", {"start": v(15, 92.25) * mm, "end": v(15, 104.25) * mm});
            skArc(sketch, "E85", {"start": v(15, 104.25) * mm, "mid": v(0, 119.25) * mm, "end": v(-15, 104.25) * mm});
            skLineSegment(sketch, "E86", {"start": v(-74.25, 0) * mm, "end": v(74.25, 0) * mm, "construction": true});
            skArc(sketch, "E87.MirrorCS", {"start": v(15, -104.25) * mm, "mid": v(0, -119.25) * mm, "end": v(-15, -104.25) * mm});
            skLineSegment(sketch, "E88.MirrorCS", {"start": v(0, -74.25) * mm, "end": v(0, -104.25) * mm, "construction": true});
            skCircle(sketch, "E89.MirrorC", {"center": v(0, -104.25) * mm, "radius": 6 * mm});
            skLineSegment(sketch, "E90.MirrorCS", {"start": v(15, -92.25) * mm, "end": v(15, -104.25) * mm});
            skLineSegment(sketch, "E91.MirrorCS", {"start": v(33, -74.25) * mm, "end": v(15, -92.25) * mm});
            skLineSegment(sketch, "E92.MirrorCS", {"start": v(-15, -92.25) * mm, "end": v(-15, -104.25) * mm});
            skLineSegment(sketch, "E93.MirrorCS", {"start": v(-33, -74.25) * mm, "end": v(-15, -92.25) * mm});
            skSolve(sketch);
        }
        {
            var Q0;
            Q0=makeQuery(id+"F16.imprint","IMPRINT",FACE,{"disambiguationData":[TD([[makeQuery(id+"F16.imprint","IMPRINT",EDGE,{"derivedFrom":sQuery(id+"F16.wireOp",EDGE,"E80")}),-1.0]])]});
            var Q1;
            Q1=makeQuery(id+"F16.imprint","IMPRINT",FACE,{"disambiguationData":[TD([[makeQuery(id+"F16.imprint","IMPRINT",EDGE,{"derivedFrom":sQuery(id+"F16.wireOp",EDGE,"E87.MirrorCS")}),-1.0]])]});
            var Q2;
            Q2=makeQuery(id+"F16.imprint","IMPRINT",FACE,{"disambiguationData":[TD([[makeQuery(id+"F16.imprint","IMPRINT",EDGE,{"derivedFrom":makeQuery(id+"F1.opExtrude","CAP_EDGE",EDGE,{"disambiguationData":[OSD([sQuery(id+"F0.wireOp",EDGE,"E1.left")])],"isStart":true})}),-1.0]])]});
            extrude(context, id + "F17", {"entities" : qUnion([Q0, Q1, Q2]), "depth" : 3 * mm});
        }
    });
